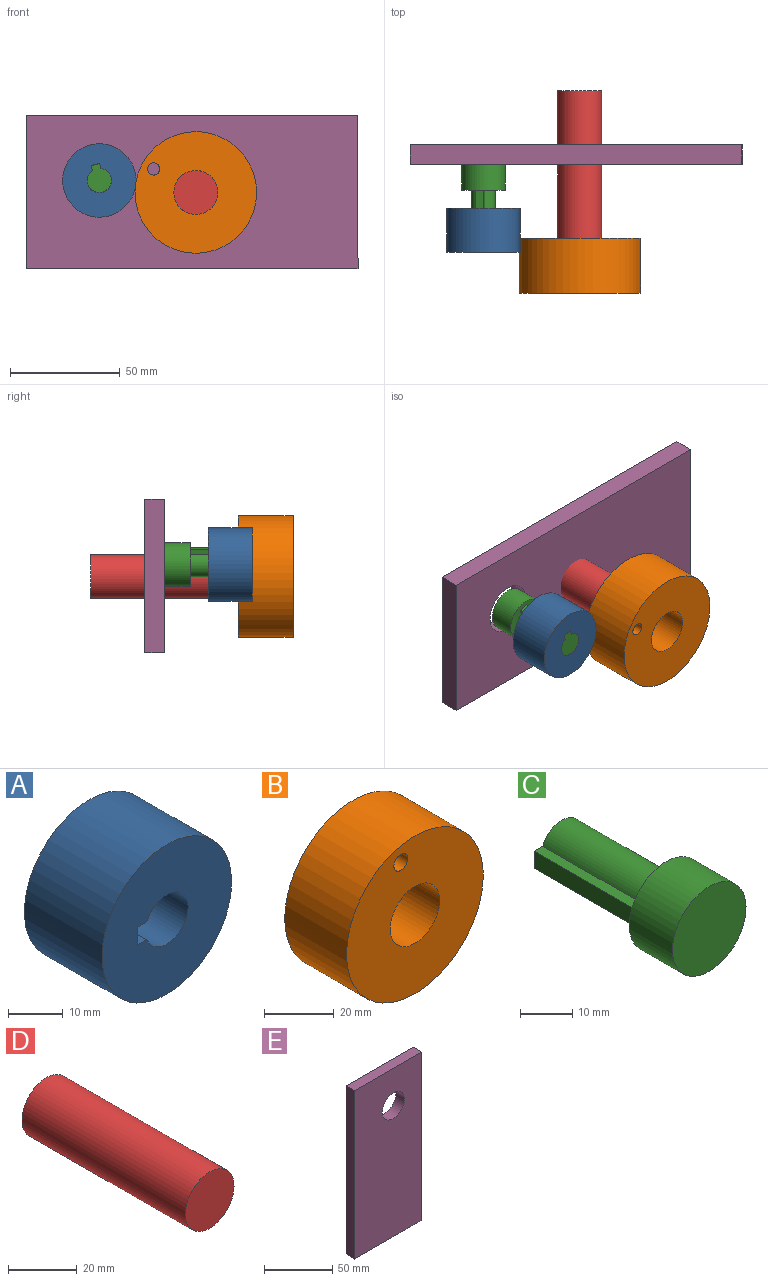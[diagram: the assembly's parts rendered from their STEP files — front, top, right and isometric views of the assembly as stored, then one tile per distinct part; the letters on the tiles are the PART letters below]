
ASSEMBLY  parts=5 mates=4
PART A: 7 faces, bbox 33.4x20x33.4 mm
  f0: plane 33.41x33.41mm, normal (0,-1,0), area 773.3mm2, adj f2,f3,f4,f5,f6
  f1: plane 33.41x33.41mm, normal (0,1,0), area 773.3mm2, adj f2,f3,f4,f5,f6
  f2: cylinder r=16.71mm len=33.41mm, axis (0,1,0), area 2099.4mm2, adj f0,f1
  f3: plane 20x2.38mm, normal (0,0,-1), area 47.5mm2, adj f0,f1,f4,f6
  f4: plane 20x4mm, normal (1,0,0), area 80mm2, adj f0,f1,f3,f5
  f5: plane 20x2.38mm, normal (0,0,1), area 47.5mm2, adj f0,f1,f4,f6
  f6: cylinder r=5.5mm len=20mm, axis (0,-1,0), area 609.3mm2, adj f0,f1,f3,f5
PART B: 5 faces, bbox 55.2x25x55.2 mm
  f0: cylinder r=10mm len=25mm, axis (0,-1,0), area 1570.8mm2, adj f2,f3
  f1: cylinder r=27.62mm len=55.24mm, axis (0,-1,0), area 4338.6mm2, adj f2,f3
  f2: plane 55.24x55.24mm, normal (0,1,0), area 2058.1mm2, adj f0,f1,f4
  f3: plane 55.24x55.24mm, normal (0,-1,0), area 2058.1mm2, adj f0,f1,f4
  f4: cylinder r=2.78mm len=25mm, axis (0,-1,0), area 437.4mm2, adj f2,f3
PART C: 8 faces, bbox 19.9x40x19.9 mm
  f0: plane 28.3x4mm, normal (-1,0,0), area 113.2mm2, adj f1,f3,f4,f6
  f1: plane 28.3x2.38mm, normal (0,0,-1), area 67.3mm2, adj f0,f2,f4,f6
  f2: cylinder r=5.5mm len=28.3mm, axis (0,1,0), area 862.1mm2, adj f1,f3,f4,f6
  f3: plane 28.3x2.38mm, normal (0,0,1), area 67.3mm2, adj f0,f2,f4,f6
  f4: plane 13x11mm, normal (0,1,0), area 103.5mm2, adj f0,f1,f2,f3
  f5: cylinder r=9.97mm len=19.93mm, axis (0,-1,0), area 732.6mm2, adj f6,f7
  f6: plane 19.93x19.93mm, normal (0,1,0), area 208.5mm2, adj f0,f1,f2,f3,f5
  f7: plane 19.93x19.93mm, normal (0,-1,0), area 312mm2, adj f5
PART D: 3 faces, bbox 20x67x20 mm
  f0: cylinder r=10mm len=67mm, axis (0,-1,0), area 4209.7mm2, adj f1,f2
  f1: plane 20x20mm, normal (0,1,0), area 314.2mm2, adj f0
  f2: plane 20x20mm, normal (0,-1,0), area 314.2mm2, adj f0
PART E: 7 faces, bbox 69.8x9x151 mm
  f0: plane 150.97x9mm, normal (-1,0,0), area 1358.7mm2, adj f2,f3,f4,f5
  f1: plane 150.97x9mm, normal (1,0,0), area 1358.7mm2, adj f2,f3,f4,f5
  f2: plane 69.76x9mm, normal (0,0,-1), area 627.9mm2, adj f0,f1,f3,f4
  f3: plane 150.97x69.76mm, normal (0,1,0), area 10118.2mm2, adj f0,f1,f2,f5,f6
  f4: plane 150.97x69.76mm, normal (0,-1,0), area 10118.2mm2, adj f0,f1,f2,f5,f6
  f5: plane 69.76x9mm, normal (0,0,1), area 627.9mm2, adj f0,f1,f3,f4
  f6: cylinder r=11.48mm len=22.95mm, axis (0,-1,0), area 649mm2, adj f3,f4
PLACE A rot(axis=(0,1,0),75.9deg) t=(-2.74,-296.44,26.09)mm
PLACE B rot(axis=(0.62,0,-0.79),180deg) t=(41.1,-288.64,20.62)mm
PLACE C rot(axis=(0.79,0,-0.62),180deg) t=(-2.73,-354.14,26.02)mm
PLACE D rot(axis=(0,-1,0),90deg) t=(41.1,-416.24,20.62)mm
PLACE E rot(axis=(0,-1,0),90deg) t=(87.58,-347.74,11.25)mm
MATE fastened C.f2 <-> A.f0  axis (0,-1,0) through (-2.73,-316.44,26.02)mm
MATE revolute E.f6 <-> C.f5  axis (0,-1,0) through (-2.73,-276.44,26.02)mm
MATE fastened E.f4 <-> D.f0  axis (0,-1,0) through (41.1,-276.44,20.62)mm
MATE revolute B.f1 <-> D.f0  axis (0,1,0) through (41.1,-309.94,20.62)mm
